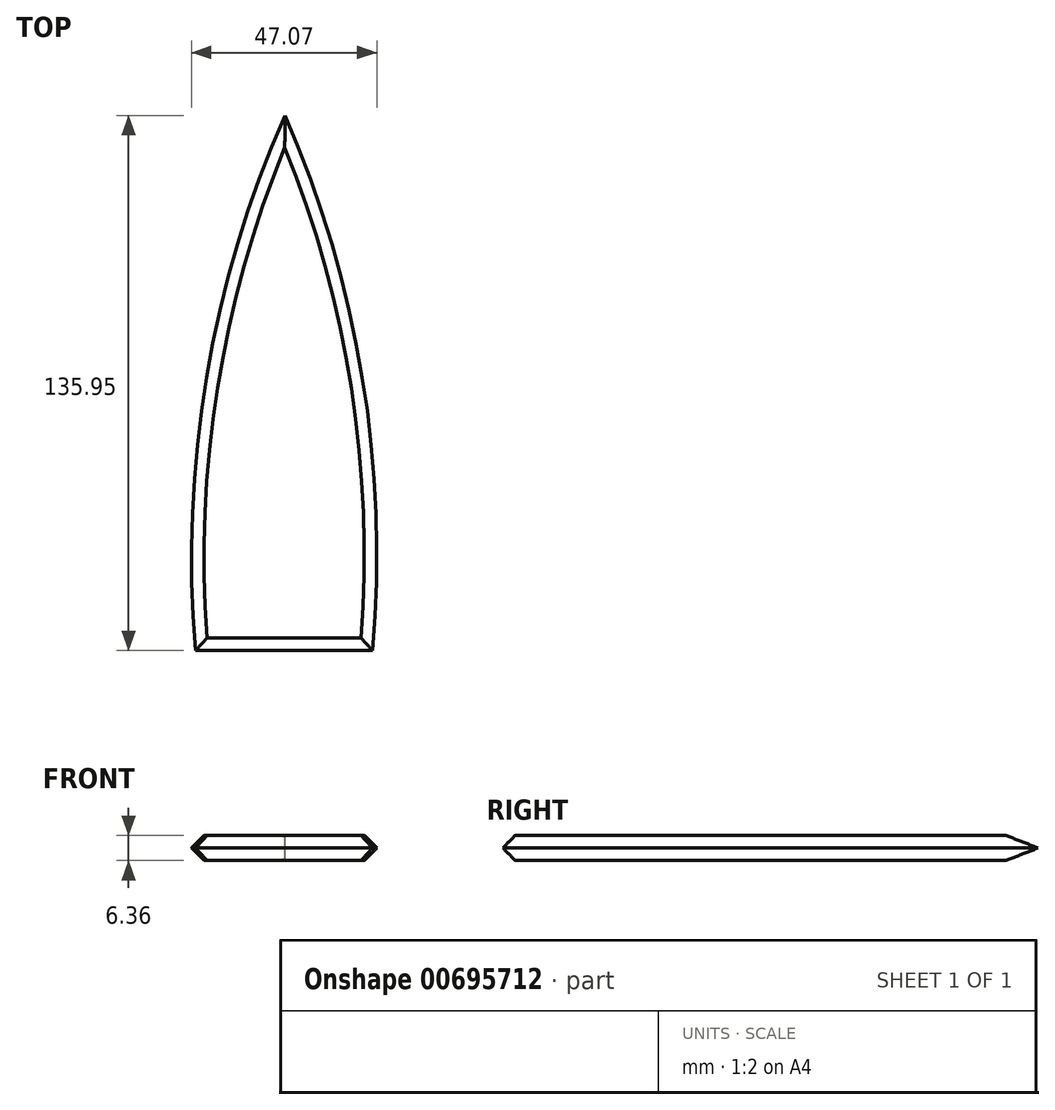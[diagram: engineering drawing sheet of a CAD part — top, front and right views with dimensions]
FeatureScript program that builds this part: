
annotation { "Feature Type Name" : "Feature", "Feature Type Description" : "" }
export const myFeature = defineFeature(function(context is Context, id is Id, definition is map)
    precondition{}
    {
        {
            var Q0;
            Q0=qCreatedBy(makeId("Top.planeOp"),FACE);
            var sketch = newSketch(context, id + "F0", { "sketchPlane" : qUnion([Q0])});
            skArc(sketch, "E0", {"start": v(0, 75.83) * mm, "mid": v(-19.88, 9.28) * mm, "end": v(-22.74, -60.12) * mm});
            skArc(sketch, "E1", {"start": v(22.32, -60.12) * mm, "mid": v(19.67, 9.25) * mm, "end": v(0, 75.83) * mm});
            skLineSegment(sketch, "E2", {"start": v(-22.74, -60.12) * mm, "end": v(22.32, -60.12) * mm});
            skSolve(sketch);
        }
        {
            var Q0;
            Q0=makeQuery(id+"F0.imprint","IMPRINT",FACE,{"disambiguationData":[TD([[makeQuery(id+"F0.imprint","IMPRINT",EDGE,{"derivedFrom":sQuery(id+"F0.wireOp",EDGE,"E0")}),1.0]])]});
            extrude(context, id + "F1", {"entities" : qUnion([Q0]), "endBound" : BoundingType.SYMMETRIC, "depth" : 6.35 * mm, "offsetDistance" : 25.4 * mm});
        }
        {
            var Q0;
            Q0=makeQuery(id+"F1.opExtrude","CAP_FACE",FACE,{"disambiguationData":[OSD([sQuery(id+"F0.wireOp",EDGE,"E0"),sQuery(id+"F0.wireOp",EDGE,"E1"),sQuery(id+"F0.wireOp",EDGE,"E2")])],"isStart":false});
            var Q1;
            Q1=makeQuery(id+"F1.opExtrude","CAP_FACE",FACE,{"disambiguationData":[OSD([sQuery(id+"F0.wireOp",EDGE,"E0"),sQuery(id+"F0.wireOp",EDGE,"E1"),sQuery(id+"F0.wireOp",EDGE,"E2")])],"isStart":true});
            chamfer(context, id + "F2", {"entities" : qUnion([Q0, Q1]), "width" : 3.17 * mm, "tangentPropagation" : true});
        }
    });
